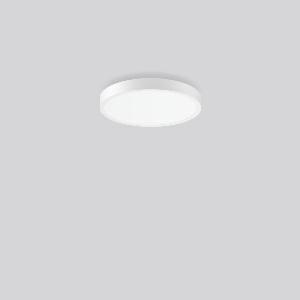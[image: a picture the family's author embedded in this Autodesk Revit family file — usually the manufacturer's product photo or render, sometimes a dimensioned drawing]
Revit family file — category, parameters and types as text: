
# Revit family: triona_round_a_312420_002_1_730_3da0
name_source: partatom
category: Lighting Fixtures
units: mm (PartAtom-declared; Revit-internal decimal feet)

## family parameters
Cut with Voids When Loaded = No
Host = Face
Light Source = No
Part Type = Normal
Room Calculation Point = No
Round Connector Dimension = Use Diameter
Shared = No

## types (1)
- TRIONA round A (1 x LED Modul 840, 6050 lm, 4000)
    Apparent Load = 64 VA
    CIE Flux Codes = 49 80 96 82 100
    Color Rendering = 80
    Color Temperature = 4000
    Default Elevation = 1800 mm
    Description = Series: TRIONA round
Decorative round LED surface-mounted luminaire. Flat, seamless frame: aluminium extrusion profile, powder coated. Cover made of sheet steel, powder-coated. Direct light emission through a diffuser plastic opal. Indirect light emission through a flush diffuser made of satin-finish plastic. Lightguide and diffuser made of non-yellowing plastic (PMMA). Lateral light emission (RZB SIDELITE technology) for above-average homogeneous light distribution. Direct 70%, indirect 30% light emission. Suitable for Ceiling mounting, Wall (surface). Tool-free mounting via bayonet connection. Electronic ballast included. Very easy installation thanks to Plug+Play connection. With Casambi smart+free Bluetooth control for wireless network and operation using Android / iOS devices, free app available for download. 
Colour: traffic white, matt (RAL 9016)
Diameter: 461 mm
Height: 88 mm
Lamp: LED
Socket: without socket
Colour temperature: 4000K
Colour rendering index (CRI): 80
System power: 64 W
Rated luminous flux: 6050 lm
Luminous efficiency: 95 lm/W
Control gear: Dimmable Bluetooth converter
Protection class: I
Type of protection: IP 20
    Height = 88 mm
    Lamp = 1 x LED Modul 840
    Lamp Light Flux = 6050 lm
    Lamp count = 1
    Length = 461 mm
    Lifetime = 50000 h
    Luminous efficacy = 95 lm/W
    Manufacturer = RZB
    ModVariant = No
    Model = 312420.002.1.730
    Mounting Place = Ceiling
    Mounting Type = Surface mounted
    Number of Poles = 1
    OnlyDefault = Yes
    Power Factor = 1
    Product Name = TRIONA round A
    Product group = Surface mounted modular luminaires
    ProductGroupID = 306
    Protection Class = Protection class I
    Protection Degree = IP 20
    RLX_Detail_Level = 1
    RLX_Emergency_Light_Flux = 0 lm
    RLX_Emergency_Type = 0
    RLX_Emergency_Type_DB = No
    RlxData = <blob elided: 36789 chars, md5=4d97b946>
    Socket = socket
    Standby Power = 0 W
    System Light Flux = 6050 lm
    System Power = 64 W
    Type Comments = Product without accessories
    Type Image = 312420.002.jpg
    URL = http://relux.com
    VarID = ---
    Voltage = 230 V
    Voltage Range = 220-240 V
    Weight = 0.00 kg
    Width = 0 mm  [stored 0 ft]

note: [stored X ft] marks values corroborated as IEEE doubles in the binary element streams (Revit-internal decimal feet)

## geometry (parser evidence)
native form markers: Blend x4, Sweep x14
no freeform markers — native parametric forms only
